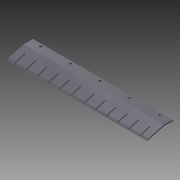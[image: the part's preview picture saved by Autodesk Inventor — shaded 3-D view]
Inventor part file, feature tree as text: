
AUTODESK INVENTOR PART (.ipt)
format: ipt  version: 2014 (Build 180170000, 170)  size: 317,952 bytes
history: native  units: mm
features: other x6, sketch x5, hole x2, extrude x1
ambient origin geometry x8: Origin, YZ Plane, XZ Plane, XY Plane, X Axis, Y Axis, Z Axis, Center Point
bodies: Body1 (feature_tree)
feature tree (14):
  other  "Sólido1"
  other  "Cara1"
  other  "Pliegue1"
  extrude  "Extrusión1"  Depth=200.0mm
  hole  "Agujero1"  [1 undecoded]
  sketch  "Boceto1"  dims[d0=100.0mm d1=200.0mm]
  other  "Placa1"
  sketch  "Boceto2"  dims[d2=38.0mm d3=13.0mm]
  sketch  "Boceto3"  dims[d4=1.5mm d5=25.0mm]
  sketch  "Boceto5"  dims[d6=1.5mm]
  sketch  "Boceto6"  dims[d7=0.75mm d8=3.0mm d9=1.5mm d10=15.0deg d11=1.0mm d12=1.0mm d13=1.5mm d14=10.0mm d16=1.0mm d17=1.5mm d18=15.0mm d19=10.0mm d20=1.0mm d21=1.5mm d23=1.0mm d24=1.5mm d25=15.0mm d26=15.0mm d27=15.0mm d28=1.0mm d29=1.5mm d31=15.0mm d32=1.0mm d33=1.5mm d35=15.0mm d38=1.0mm d39=1.5mm d41=1.0mm d42=1.5mm d44=15.0mm d45=1.0mm d46=1.5mm d48=15.0mm d49=15.0mm d50=1.0mm d51=1.5mm d53=1.0mm d54=1.5mm d56=15.0mm d57=1.0mm d58=1.5mm d60=15.0mm d61=15.0mm d62=1.5mm d63=0.0mm d65=15.0mm d66=15.0mm d67=15.0mm d68=15.0mm d69=15.0mm d70=15.0mm d71=15.0mm d72=15.0mm d73=15.0mm d74=15.0mm d103=10.0mm d104=0.0mm d105=60.0deg d106=3.4mm d107=6.0mm d108=4.0mm d109=2.0mm d110=90.0deg d111=8.0mm d112=0.0mm]
  hole  "Hole3"  [1 undecoded]
  other  "Cortar2"
  other  "Definición1"
note: 2 required parameter values undecoded (feature->parameter linkage not recoverable at this tier; creation-order binding heuristic only, values carry confidence <= 0.55)
